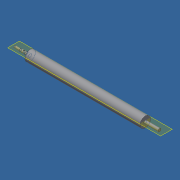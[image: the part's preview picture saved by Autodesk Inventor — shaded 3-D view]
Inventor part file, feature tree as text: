
AUTODESK INVENTOR PART (.ipt)
format: ipt  version: 2021 (Build 250183000, 183)  size: 105,984 bytes
history: native  units: in
note: dims shown in document units (in); Inventor stores cm internally (conversion verified against a paired STEP export)
features: extrude x6, sketch x6, plane x1
ambient origin geometry x8: Origin, YZ Plane, XZ Plane, XY Plane, X Axis, Y Axis, Z Axis, Center Point
bodies: Solid1 (feature_tree)
feature tree (13):
  extrude  "Extrusion1"  Depth=8.937in TaperAngle=0.0deg
  sketch  "Sketch2"  dims[d3=0.2362in d4=0.2362in]
  extrude  "Extrusion2"  Depth=0.2362in
  extrude  "Extrusion3"  Depth=0.315in TaperAngle=0.0deg
  extrude  "Extrusion4"  Depth=0.4331in TaperAngle=0.0deg
  plane  "Work Plane1"
  extrude  "Extrusion5"  Depth=0.0787in
  extrude  "Extrusion6"  Depth=0.1575in
  sketch  "Sketch1"  dims[d0=0.8268in d1=8.937in d2=0.0in]
  sketch  "Sketch3"  dims[d5=0.315in d6=0.0in d7=1.1024in d8=0.0in]
  sketch  "Sketch4"  dims[d9=0.1969in d10=0.4331in d11=0.0in]
  sketch  "Sketch5"  dims[d12=0.0787in d13=0.1575in]
  sketch  "Sketch6"  dims[d14=0.1378in d15=0.0in d16=0.1575in d17=0.4331in d18=0.0in d19=0.3346in d20=0.0in]
